# Revit family: 4.Водяной нагреватель для прямоугольных каналов WWN
name_source: partatom
category: Оборудование
revit_build: Autodesk Revit 2016 (Build: 20151209_0715(x64)
units: mm (PartAtom-declared; Revit-internal decimal feet)

## family parameters
Всегда вертикально = Да
На основе рабочей плоскости = Нет
Общий = Нет
При загрузке вырезать с полостями = Нет
Размер круглого соединителя = Использовать диаметр
Тип детали = Нормальный
Точка расчета площади = Нет

## types (20) — shared parameters
d = 25 мм
d1 = 10 мм
Глубина среза = 15 мм
Единица измерения = шт.
Завод изготовитель = KORF
Ключевая пометка = Вентиляция
Материал = Сталь серая
Наименование и тех.хар-ка = Водяной нагреватель для прямоугольных каналов
Раздел = ОВ

## per-type parameters (varying)
| type | А | Б | Высота | Г | Д | Е | Ж | Заправочный объем, л | И | И1 | К | Масса единицы | Размер В | Тип, марка, обозначение | Ширина |
| 30-15/2 | 300 мм | 150 мм | 150 мм | 170 мм | 340 мм | 190 мм | 9 мм | 0.5 м³ | 164 мм | 160 мм | 432 мм | 4.1 кг | 320 мм | WWN 30-15/2 | 300 мм |
| 30-15/3 | 300 мм | 150 мм | 150 мм | 170 мм | 340 мм | 190 мм | 9 мм | 0.6 м³ | 192 мм | 188 мм | 432 мм | 5.6 кг | 320 мм | WWN 30-15/2 | 300 мм |
| 40-20/2 | 400 мм | 200 мм | 200 мм | 220 мм | 440 мм | 240 мм | 9 мм | 0.7 м³ | 164 мм | 160 мм | 532 мм | 5.6 кг | 420 мм | WWN 40-20/2 | 400 мм |
| 40-20/3 | 400 мм | 200 мм | 200 мм | 220 мм | 440 мм | 240 мм | 9 мм | 1 м³ | 192 мм | 188 мм | 532 мм | 7.1 кг | 420 мм | WWN 40-20/3 | 400 мм |
| 50-25/2 | 500 мм | 250 мм | 250 мм | 270 мм | 540 мм | 290 мм | 9 мм | 1 м³ | 164 мм | 160 мм | 632 мм | 6.6 кг | 520 мм | WWN 50-25/2 | 500 мм |
| 50-25/3 | 500 мм | 250 мм | 250 мм | 270 мм | 540 мм | 290 мм | 9 мм | 1.4 м³ | 192 мм | 188 мм | 632 мм | 8.6 кг | 520 мм | WWN 50-25/3 | 500 мм |
| 50-30/2 | 500 мм | 300 мм | 300 мм | 320 мм | 540 мм | 340 мм | 9 мм | 1.3 м³ | 164 мм | 160 мм | 632 мм | 7.1 кг | 520 мм | WWN 50-30/2 | 500 мм |
| 50-30/3 | 500 мм | 300 мм | 300 мм | 320 мм | 540 мм | 340 мм | 9 мм | 1.8 м³ | 192 мм | 188 мм | 632 мм | 10.1 кг | 520 мм | WWN 50-30/3 | 500 мм |
| 60-30/2 | 600 мм | 300 мм | 300 мм | 320 мм | 640 мм | 340 мм | 9 мм | 1.5 м³ | 164 мм | 160 мм | 732 мм | 8.1 кг | 620 мм | WWN 60-30/2 | 600 мм |
| 60-30/3 | 600 мм | 300 мм | 300 мм | 320 мм | 640 мм | 340 мм | 9 мм | 2 м³ | 192 мм | 188 мм | 732 мм | 11.6 кг | 620 мм | WWN 60-30/3 | 600 мм |
| 60-35/2 | 600 мм | 350 мм | 350 мм | 370 мм | 640 мм | 390 мм | 9 мм | 1.7 м³ | 164 мм | 160 мм | 732 мм | 8.8 кг | 620 мм | WWN 60-35/2 | 600 мм |
| 60-35/3 | 600 мм | 350 мм | 350 мм | 370 мм | 640 мм | 390 мм | 9 мм | 2.3 м³ | 192 мм | 188 мм | 732 мм | 13.1 кг | 620 мм | WWN 60-35/3 | 600 мм |
| 70-40/2 | 700 мм | 400 мм | 400 мм | 420 мм | 740 мм | 440 мм | 9 мм | 2.2 м³ | 164 мм | 160 мм | 832 мм | 10.6 кг | 720 мм | WWN 70-40/2 | 700 мм |
| 70-40/3 | 700 мм | 400 мм | 400 мм | 420 мм | 740 мм | 440 мм | 9 мм | 3 м³ | 192 мм | 188 мм | 832 мм | 14.6 кг | 720 мм | WWN 70-40/3 | 700 мм |
| 80-50/2 | 800 мм | 500 мм | 500 мм | 520 мм | 840 мм | 540 мм | 9 мм | 3.2 м³ | 164 мм | 160 мм | 932 мм | 13.5 кг | 820 мм | WWN 80-50/2 | 800 мм |
| 80-50/3 | 800 мм | 500 мм | 500 мм | 520 мм | 840 мм | 540 мм | 9 мм | 4.4 м³ | 192 мм | 188 мм | 932 мм | 16.1 кг | 820 мм | WWN 80-50/3 | 800 мм |
| 90-50/2 | 900 мм | 500 мм | 500 мм | 530 мм | 960 мм | 560 мм | 11 мм | 3.5 м³ | 164 мм | 160 мм | 1042 мм | 16.4 кг | 930 мм | WWN 90-50/2 | 900 мм |
| 90-50/3 | 900 мм | 500 мм | 500 мм | 530 мм | 960 мм | 560 мм | 11 мм | 4.8 м³ | 192 мм | 188 мм | 1042 мм | 17.6 кг | 930 мм | WWN 90-50/3 | 900 мм |
| 100-50/2 | 1000 мм | 500 мм | 500 мм | 530 мм | 1060 мм | 560 мм | 11 мм | 3.8 м³ | 164 мм | 160 мм | 1142 мм | 18.5 кг | 1030 мм | WWN 100-50/2 | 1000 мм |
| 100-50/3 | 1000 мм | 500 мм | 500 мм | 530 мм | 1060 мм | 560 мм | 11 мм | 5.3 м³ | 192 мм | 188 мм | 1142 мм | 19.8 кг | 1030 мм | WWN 100-50/3 | 1000 мм |
